# Revit family: 2200_Series_Aluminum_Mailboxes_Rack_Ladder_Units
name_source: partatom
category: Specialty Equipment
revit_build: Autodesk Revit 2016 (Build: 20150714_1515(x64)
units: mm (PartAtom-declared; Revit-internal decimal feet)

## family parameters
Always vertical = Yes
Cut with Voids When Loaded = No
OmniClass Number = 23.40.90.14.11
OmniClass Title = Mail Boxes
Part Type = Normal
Room Calculation Point = No
Round Connector Dimension = Use Diameter
Shared = No
Work Plane-Based = No

## types (10) — shared parameters
Assembly Code = C1030910
Back Enclosure Material = Steel - Salsbury Finish - Clear
Box Offset = 0.156 "
Depth = 15.5 "
Front Panel Material = Aluminum - Salsbury Finish - Aluminum
Height = 12.188 "
Lock Material = Stainless Steel -Salsbury Finish - Polished
Manufacturer = Salsbury Industries
MasterFormat Number = 10 55 00
MasterFormat Title = Postal Specialties
OmniClass 23 Number = 23.40.90.14.11
OmniClass 23 Title = Mail Boxes
Trim Material = Steel - Salsbury Finish - Black
URL = www.mailboxes.com
Version = 2.0 (06/30/18)
Width = 23.25 "

## per-type parameters (varying)
- 2212: Back Panel=No; Description=Rack Ladder System - 12 #1 Doors; Divider 3=Yes; Divider 3 Parcel=No; Dividers 1, 2, 4, 5=Yes; Dividers 6, 7=No; Door Divider Offset=0 "; Door Location D1=Rack Ladder #1 Door : #1 Door; Door Location D10=Rack Ladder #1 Door : #1 Door; Door Location D11=Rack Ladder #1 Door : #1 Door; Door Location D12=Rack Ladder #1 Door : #1 Door; Door Location D13=Rack Ladder None : No Door; Door Location D14=Rack Ladder None : No Door; Door Location D15=Rack Ladder None : No Door; Door Location D16=Rack Ladder None : No Door; Door Location D17=Rack Ladder None : No Door; Door Location D2=Rack Ladder #1 Door : #1 Door; Door Location D3=Rack Ladder #1 Door : #1 Door; Door Location D4=Rack Ladder #1 Door : #1 Door; Door Location D5=Rack Ladder #1 Door : #1 Door; Door Location D6=Rack Ladder #1 Door : #1 Door; Door Location D7=Rack Ladder #1 Door : #1 Door; Door Location D8=Rack Ladder #1 Door : #1 Door; Door Location D9=Rack Ladder #1 Door : #1 Door; Horizontal Dividers=Yes; Model=2212; Rear Door=No; Rear Overhang=Yes; Type Comments=Aluminum Mailbox; Visible=Yes; Void 1 Offset=0 "; Void 2 Offset=0 "
- 2208: Back Panel=No; Description=Rack Ladder System - 8 #2 Doors; Divider 3=Yes; Divider 3 Parcel=No; Dividers 1, 2, 4, 5=No; Dividers 6, 7=Yes; Door Divider Offset=0 "; Door Location D1=Rack Ladder None : No Door; Door Location D10=Rack Ladder None : No Door; Door Location D11=Rack Ladder None : No Door; Door Location D12=Rack Ladder #2 Door : #2 Door; Door Location D13=Rack Ladder #2 Door : #2 Door; Door Location D14=Rack Ladder #2 Door : #2 Door; Door Location D15=Rack Ladder #2 Door : #2 Door; Door Location D16=Rack Ladder #2 Door : #2 Door; Door Location D17=Rack Ladder None : No Door; Door Location D2=Rack Ladder None : No Door; Door Location D3=Rack Ladder #2 Door : #2 Door; Door Location D4=Rack Ladder None : No Door; Door Location D5=Rack Ladder None : No Door; Door Location D6=Rack Ladder #2 Door : #2 Door; Door Location D7=Rack Ladder None : No Door; Door Location D8=Rack Ladder None : No Door; Door Location D9=Rack Ladder #2 Door : #2 Door; Horizontal Dividers=Yes; Model=2208; Rear Door=No; Rear Overhang=Yes; Type Comments=Aluminum Mailbox; Visible=Yes; Void 1 Offset=0 "; Void 2 Offset=0 "
- 2204: Back Panel=No; Description=Rack Ladder System - 4 #3 Doors; Divider 3=Yes; Divider 3 Parcel=No; Dividers 1, 2, 4, 5=No; Dividers 6, 7=No; Door Divider Offset=0 "; Door Location D1=Rack Ladder None : No Door; Door Location D10=Rack Ladder None : No Door; Door Location D11=Rack Ladder None : No Door; Door Location D12=Rack Ladder #3 Door : #3 Door; Door Location D13=Rack Ladder None : No Door; Door Location D14=Rack Ladder None : No Door; Door Location D15=Rack Ladder None : No Door; Door Location D16=Rack Ladder None : No Door; Door Location D17=Rack Ladder None : No Door; Door Location D2=Rack Ladder None : No Door; Door Location D3=Rack Ladder #3 Door : #3 Door; Door Location D4=Rack Ladder None : No Door; Door Location D5=Rack Ladder None : No Door; Door Location D6=Rack Ladder #3 Door : #3 Door; Door Location D7=Rack Ladder None : No Door; Door Location D8=Rack Ladder None : No Door; Door Location D9=Rack Ladder #3 Door : #3 Door; Horizontal Dividers=Yes; Model=2204; Rear Door=No; Rear Overhang=Yes; Type Comments=Aluminum Mailbox; Visible=Yes; Void 1 Offset=0 "; Void 2 Offset=0 "
- 2202: Back Panel=No; Description=Rack Ladder System - 2 #4 Doors; Divider 3=Yes; Divider 3 Parcel=No; Dividers 1, 2, 4, 5=No; Dividers 6, 7=No; Door Divider Offset=0 "; Door Location D1=Rack Ladder None : No Door; Door Location D10=Rack Ladder None : No Door; Door Location D11=Rack Ladder None : No Door; Door Location D12=Rack Ladder #4 Door : #4 Door; Door Location D13=Rack Ladder None : No Door; Door Location D14=Rack Ladder None : No Door; Door Location D15=Rack Ladder None : No Door; Door Location D16=Rack Ladder None : No Door; Door Location D17=Rack Ladder None : No Door; Door Location D2=Rack Ladder None : No Door; Door Location D3=Rack Ladder None : No Door; Door Location D4=Rack Ladder None : No Door; Door Location D5=Rack Ladder None : No Door; Door Location D6=Rack Ladder None : No Door; Door Location D7=Rack Ladder None : No Door; Door Location D8=Rack Ladder None : No Door; Door Location D9=Rack Ladder #4 Door : #4 Door; Horizontal Dividers=No; Model=2202; Rear Door=No; Rear Overhang=Yes; Type Comments=Aluminum Mailbox; Visible=Yes; Void 1 Offset=6.2 "; Void 2 Offset=0.04 "
- 2201: Back Panel=No; Description=Rack Ladder System - 1 Door; Divider 3=No; Divider 3 Parcel=No; Dividers 1, 2, 4, 5=No; Dividers 6, 7=No; Door Divider Offset=22.031 "; Door Location D1=Rack Ladder None : No Door; Door Location D10=Rack Ladder None : No Door; Door Location D11=Rack Ladder None : No Door; Door Location D12=Rack Ladder #4 Door-Right Keyed Door : #4 Right Keyed Door; Door Location D13=Rack Ladder None : No Door; Door Location D14=Rack Ladder None : No Door; Door Location D15=Rack Ladder None : No Door; Door Location D16=Rack Ladder None : No Door; Door Location D17=Rack Ladder #4 Door-Left Blank Door : #4 Door Left Blank Door; Door Location D2=Rack Ladder None : No Door; Door Location D3=Rack Ladder None : No Door; Door Location D4=Rack Ladder None : No Door; Door Location D5=Rack Ladder None : No Door; Door Location D6=Rack Ladder None : No Door; Door Location D7=Rack Ladder None : No Door; Door Location D8=Rack Ladder None : No Door; Door Location D9=Rack Ladder None : No Door; Horizontal Dividers=No; Model=2201; Rear Door=No; Rear Overhang=Yes; Type Comments=Aluminum Mailbox; Visible=Yes; Void 1 Offset=6.2 "; Void 2 Offset=0.04 "
- 2280: Back Panel=Yes; Description=Rack Ladder System - 1 Compartment; Divider 3=No; Divider 3 Parcel=No; Dividers 1, 2, 4, 5=No; Dividers 6, 7=No; Door Divider Offset=22.031 "; Door Location D1=Rack Ladder None : No Door; Door Location D10=Rack Ladder None : No Door; Door Location D11=Rack Ladder None : No Door; Door Location D12=Rack Ladder #4 Door-Right Mail Door-Full : #4 Door Right Mail Door - Full Slot; Door Location D13=Rack Ladder None : No Door; Door Location D14=Rack Ladder None : No Door; Door Location D15=Rack Ladder None : No Door; Door Location D16=Rack Ladder None : No Door; Door Location D17=Rack Ladder #4 Door-Left Mail Door-Full : #4 Door Left Mail Door-Full Slot; Door Location D2=Rack Ladder None : No Door; Door Location D3=Rack Ladder None : No Door; Door Location D4=Rack Ladder None : No Door; Door Location D5=Rack Ladder None : No Door; Door Location D6=Rack Ladder None : No Door; Door Location D7=Rack Ladder None : No Door; Door Location D8=Rack Ladder None : No Door; Door Location D9=Rack Ladder None : No Door; Horizontal Dividers=No; Model=2280; Rear Door=No; Rear Overhang=Yes; Type Comments=Aluminum Drop Box; Visible=Yes; Void 1 Offset=6.2 "; Void 2 Offset=0.04 "
- 2282: Back Panel=Yes; Description=Rack Ladder System - 2 Compartments; Divider 3=Yes; Divider 3 Parcel=No; Dividers 1, 2, 4, 5=No; Dividers 6, 7=No; Door Divider Offset=0 "; Door Location D1=Rack Ladder None : No Door; Door Location D10=Rack Ladder None : No Door; Door Location D11=Rack Ladder None : No Door; Door Location D12=Rack Ladder #4 Door-Mail Door-Center : #4 Door Right Mail Door-Centered Slot; Door Location D13=Rack Ladder None : No Door; Door Location D14=Rack Ladder None : No Door; Door Location D15=Rack Ladder None : No Door; Door Location D16=Rack Ladder None : No Door; Door Location D17=Rack Ladder None : No Door; Door Location D2=Rack Ladder None : No Door; Door Location D3=Rack Ladder None : No Door; Door Location D4=Rack Ladder None : No Door; Door Location D5=Rack Ladder None : No Door; Door Location D6=Rack Ladder None : No Door; Door Location D7=Rack Ladder None : No Door; Door Location D8=Rack Ladder None : No Door; Door Location D9=Rack Ladder #4 Door-Mail Door-Center : #4 Door Right Mail Door-Centered Slot; Horizontal Dividers=No; Model=2282; Rear Door=No; Rear Overhang=Yes; Type Comments=Aluminum Drop Boxes; Visible=Yes; Void 1 Offset=6.2 "; Void 2 Offset=0.04 "
- None: Back Panel=No; Description=Rack Ladder System - 12 #1 Doors; Divider 3=No; Divider 3 Parcel=No; Dividers 1, 2, 4, 5=No; Dividers 6, 7=No; Door Divider Offset=0 "; Door Location D1=Rack Ladder #1 Door : #1 Door; Door Location D10=Rack Ladder #1 Door : #1 Door; Door Location D11=Rack Ladder #1 Door : #1 Door; Door Location D12=Rack Ladder #1 Door : #1 Door; Door Location D13=Rack Ladder None : No Door; Door Location D14=Rack Ladder None : No Door; Door Location D15=Rack Ladder None : No Door; Door Location D16=Rack Ladder None : No Door; Door Location D17=Rack Ladder None : No Door; Door Location D2=Rack Ladder #1 Door : #1 Door; Door Location D3=Rack Ladder #1 Door : #1 Door; Door Location D4=Rack Ladder #1 Door : #1 Door; Door Location D5=Rack Ladder #1 Door : #1 Door; Door Location D6=Rack Ladder #1 Door : #1 Door; Door Location D7=Rack Ladder #1 Door : #1 Door; Door Location D8=Rack Ladder #1 Door : #1 Door; Door Location D9=Rack Ladder #1 Door : #1 Door; Horizontal Dividers=No; Model=2212; Rear Door=No; Rear Overhang=No; Type Comments=Aluminum Mailbox; Visible=No; Void 1 Offset=0 "; Void 2 Offset=0 "
- 2270P: Back Panel=No; Description=Rack Ladder System - 1 Door; Divider 3=No; Divider 3 Parcel=No; Dividers 1, 2, 4, 5=No; Dividers 6, 7=No; Door Divider Offset=0 "; Door Location D1=Rack Ladder None : No Door; Door Location D10=Rack Ladder None : No Door; Door Location D11=Rack Ladder None : No Door; Door Location D12=Rack Ladder #4 Door-Right Parcel Doors : Full Parcel Door; Door Location D13=Rack Ladder None : No Door; Door Location D14=Rack Ladder None : No Door; Door Location D15=Rack Ladder None : No Door; Door Location D16=Rack Ladder None : No Door; Door Location D17=Rack Ladder None : No Door; Door Location D2=Rack Ladder None : No Door; Door Location D3=Rack Ladder None : No Door; Door Location D4=Rack Ladder None : No Door; Door Location D5=Rack Ladder None : No Door; Door Location D6=Rack Ladder None : No Door; Door Location D7=Rack Ladder None : No Door; Door Location D8=Rack Ladder None : No Door; Door Location D9=Rack Ladder None : No Door; Horizontal Dividers=No; Model=2270P; Rear Door=Yes; Rear Overhang=No; Type Comments=Aluminum Parcel Locker; Visible=Yes; Void 1 Offset=6.2 "; Void 2 Offset=0.04 "
- 2272P: Back Panel=No; Description=Rack Ladder System - 2 Doors; Divider 3=No; Divider 3 Parcel=Yes; Dividers 1, 2, 4, 5=No; Dividers 6, 7=No; Door Divider Offset=0 "; Door Location D1=Rack Ladder None : No Door; Door Location D10=Rack Ladder None : No Door; Door Location D11=Rack Ladder None : No Door; Door Location D12=Rack Ladder #4 Door-Right Parcel Doors : #4 Door-Right Parcel Door 2P; Door Location D13=Rack Ladder None : No Door; Door Location D14=Rack Ladder None : No Door; Door Location D15=Rack Ladder None : No Door; Door Location D16=Rack Ladder None : No Door; Door Location D17=Rack Ladder None : No Door; Door Location D2=Rack Ladder None : No Door; Door Location D3=Rack Ladder None : No Door; Door Location D4=Rack Ladder None : No Door; Door Location D5=Rack Ladder None : No Door; Door Location D6=Rack Ladder None : No Door; Door Location D7=Rack Ladder None : No Door; Door Location D8=Rack Ladder None : No Door; Door Location D9=Rack Ladder #4 Door-Right Parcel Doors : #4 Door-Right Parcel Door 1P; Horizontal Dividers=No; Model=2272P; Rear Door=Yes; Rear Overhang=No; Type Comments=Aluminum Parcel Lockers; Visible=Yes; Void 1 Offset=6.2 "; Void 2 Offset=0.04 "

## geometry (parser evidence)
native form markers: Extrusion x1, Sweep x31
no freeform markers — native parametric forms only
